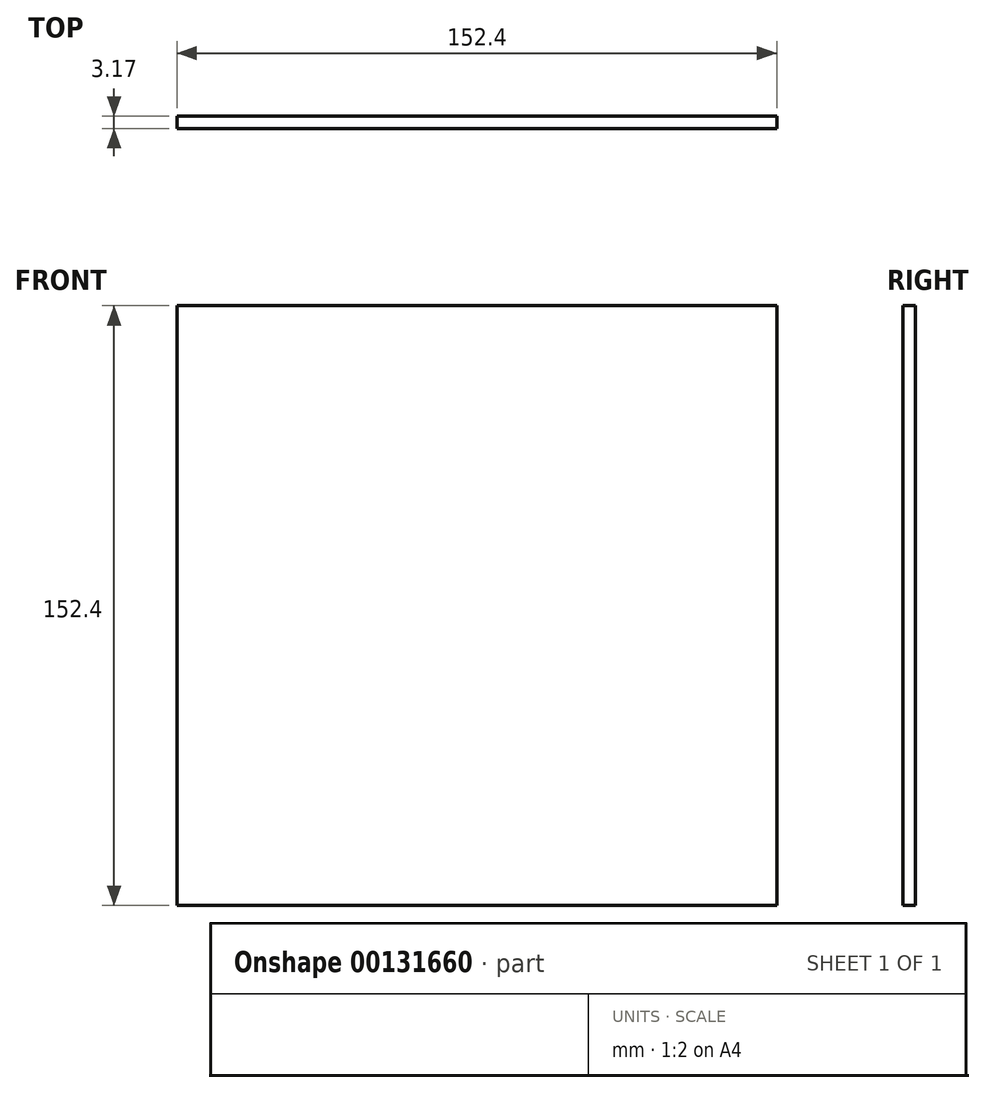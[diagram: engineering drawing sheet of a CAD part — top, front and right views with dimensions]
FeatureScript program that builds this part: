
annotation { "Feature Type Name" : "Feature", "Feature Type Description" : "" }
export const myFeature = defineFeature(function(context is Context, id is Id, definition is map)
    precondition{}
    {
        {
            var Q0;
            Q0=qCreatedBy(makeId("Front.planeOp"),FACE);
            var sketch = newSketch(context, id + "F0", { "sketchPlane" : qUnion([Q0])});
            skLineSegment(sketch, "E0.bottom", {"start": v(-112.46, 111.84) * mm, "end": v(39.94, 111.84) * mm});
            skLineSegment(sketch, "E0.top", {"start": v(-112.46, -40.56) * mm, "end": v(39.94, -40.56) * mm});
            skLineSegment(sketch, "E0.left", {"start": v(-112.46, 111.84) * mm, "end": v(-112.46, -40.56) * mm});
            skLineSegment(sketch, "E0.right", {"start": v(39.94, 111.84) * mm, "end": v(39.94, -40.56) * mm});
            skSolve(sketch);
        }
        {
            var Q0;
            Q0=makeQuery(id+"F0.imprint","IMPRINT",FACE,{"disambiguationData":[TD([[makeQuery(id+"F0.imprint","IMPRINT",EDGE,{"derivedFrom":sQuery(id+"F0.wireOp",EDGE,"E0.bottom")}),-1.0]])]});
            extrude(context, id + "F1", {"entities" : qUnion([Q0]), "depth" : 3.17 * mm});
        }
    });
